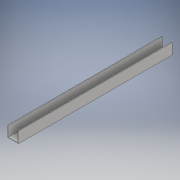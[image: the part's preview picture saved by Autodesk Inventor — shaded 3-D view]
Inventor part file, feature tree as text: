
AUTODESK INVENTOR PART (.ipt)
format: ipt  version: 2017 (Build 210142000, 142)  size: 99,840 bytes
history: native  units: in
note: dims shown in document units (in); Inventor stores cm internally (conversion verified against a paired STEP export)
features: sketch x2, extrude x1
ambient origin geometry x8: Origin, YZ Plane, XZ Plane, XY Plane, X Axis, Y Axis, Z Axis, Center Point
bodies: Solid1 (feature_tree)
feature tree (3):
  sketch  "Sketch1"  dims[d2=0.079in d3=1.26in]
  sketch  "Sketch2"  dims[d5=18.0in d6=0.0in]
  extrude  "Extrusion1"  Depth=1.26in
